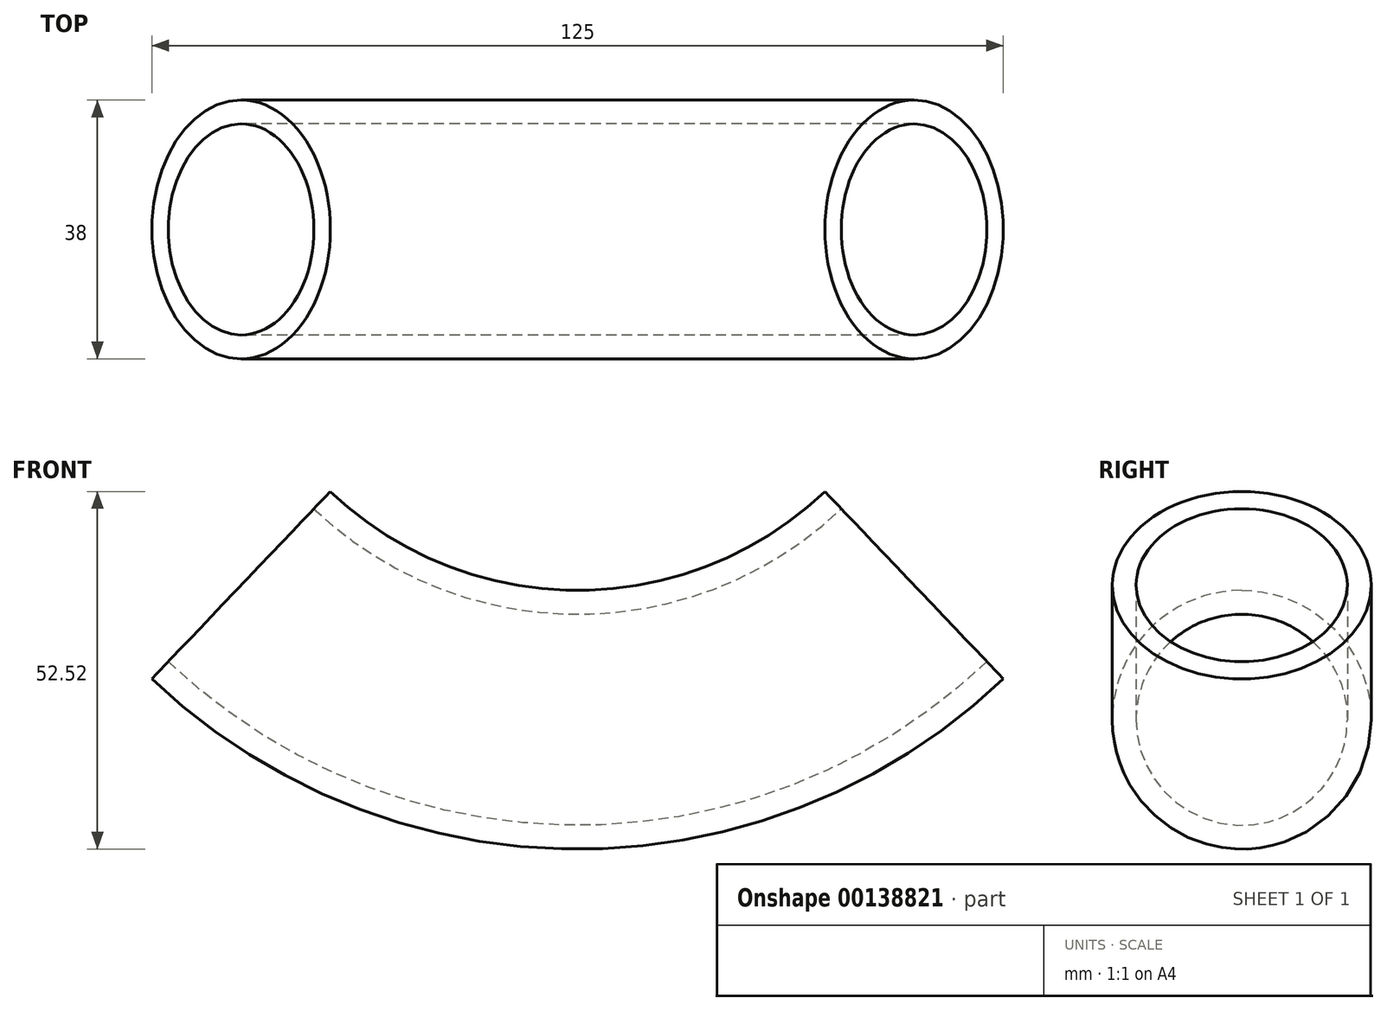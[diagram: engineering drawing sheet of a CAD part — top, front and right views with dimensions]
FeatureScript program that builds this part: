
annotation { "Feature Type Name" : "Feature", "Feature Type Description" : "" }
export const myFeature = defineFeature(function(context is Context, id is Id, definition is map)
    precondition{}
    {
        {
            var Q0;
            Q0=qCreatedBy(makeId("Front.planeOp"),FACE);
            var sketch = newSketch(context, id + "F0", { "sketchPlane" : qUnion([Q0])});
            skLineSegment(sketch, "E0.bottom", {"start": v(62.5, 12.5) * mm, "end": v(-62.5, 12.5) * mm, "construction": true});
            skLineSegment(sketch, "E0.top", {"start": v(62.5, -12.5) * mm, "end": v(-62.5, -12.5) * mm});
            skLineSegment(sketch, "E0.left", {"start": v(62.5, 12.5) * mm, "end": v(62.5, -12.5) * mm, "construction": true});
            skLineSegment(sketch, "E0.right", {"start": v(-62.5, 12.5) * mm, "end": v(-62.5, -12.5) * mm, "construction": true});
            skPoint(sketch, "E0.middle", {"position": v(0, 0) * mm});
            skCircle(sketch, "E1", {"center": v(0, 78.12) * mm, "radius": 90.62 * mm, "construction": true});
            skPoint(sketch, "E2", {"position": v(-62.5, 12.5) * mm});
            skPoint(sketch, "E3", {"position": v(62.5, 12.5) * mm});
            skPoint(sketch, "E4", {"position": v(0, -12.5) * mm});
            skLineSegment(sketch, "E5", {"start": v(0, 78.12) * mm, "end": v(-62.5, -12.5) * mm});
            skArc(sketch, "E6", {"start": v(-62.5, 12.5) * mm, "mid": v(0, -12.5) * mm, "end": v(62.5, 12.5) * mm});
            skLineSegment(sketch, "E7", {"start": v(-62.5, 12.5) * mm, "end": v(0, 78.13) * mm});
            skSolve(sketch);
        }
        {
            var Q0;
            Q0=qCreatedBy(makeId("Right.planeOp"),FACE);
            var Q1;
            Q1=sQuery(id+"F0.wireOp",VERTEX,"E2");
            cPlane(context, id + "F1", {"entities" : qUnion([Q0, Q1]), "cplaneType" : CPlaneType.PLANE_POINT, "offset" : 25 * mm, "width" : 150 * mm, "height" : 150 * mm});
        }
        {
            var Q0;
            Q0=qCreatedBy(id+"F1.planeOp",FACE);
            var Q1;
            Q1=sQuery(id+"F0.wireOp",EDGE,"E7");
            cPlane(context, id + "F2", {"entities" : qUnion([Q0, Q1]), "cplaneType" : CPlaneType.LINE_ANGLE, "offset" : 25 * mm, "angle" : 0 * degree, "width" : 150 * mm, "height" : 150 * mm});
        }
        {
            var Q0;
            Q0=qCreatedBy(id+"F2.planeOp",FACE);
            var sketch = newSketch(context, id + "F3", { "sketchPlane" : qUnion([Q0])});
            skPoint(sketch, "E8", {"position": v(0, -34.05) * mm});
            skCircle(sketch, "E9", {"center": v(0, -15.05) * mm, "radius": 19 * mm});
            skCircle(sketch, "E10", {"center": v(0, -15.05) * mm, "radius": 15.5 * mm});
            skSolve(sketch);
        }
        {
            var Q0;
            Q0=makeQuery(id+"F3.imprint","IMPRINT",FACE,{"disambiguationData":[TD([[makeQuery(id+"F3.imprint","IMPRINT",EDGE,{"derivedFrom":sQuery(id+"F3.wireOp",EDGE,"E9")}),1.0]])]});
            var Q1;
            Q1=sQuery(id+"F0.wireOp",EDGE,"E6");
            sweep(context, id + "F4", {"profiles" : qUnion([Q0]), "path" : qUnion([Q1])});
        }
    });
